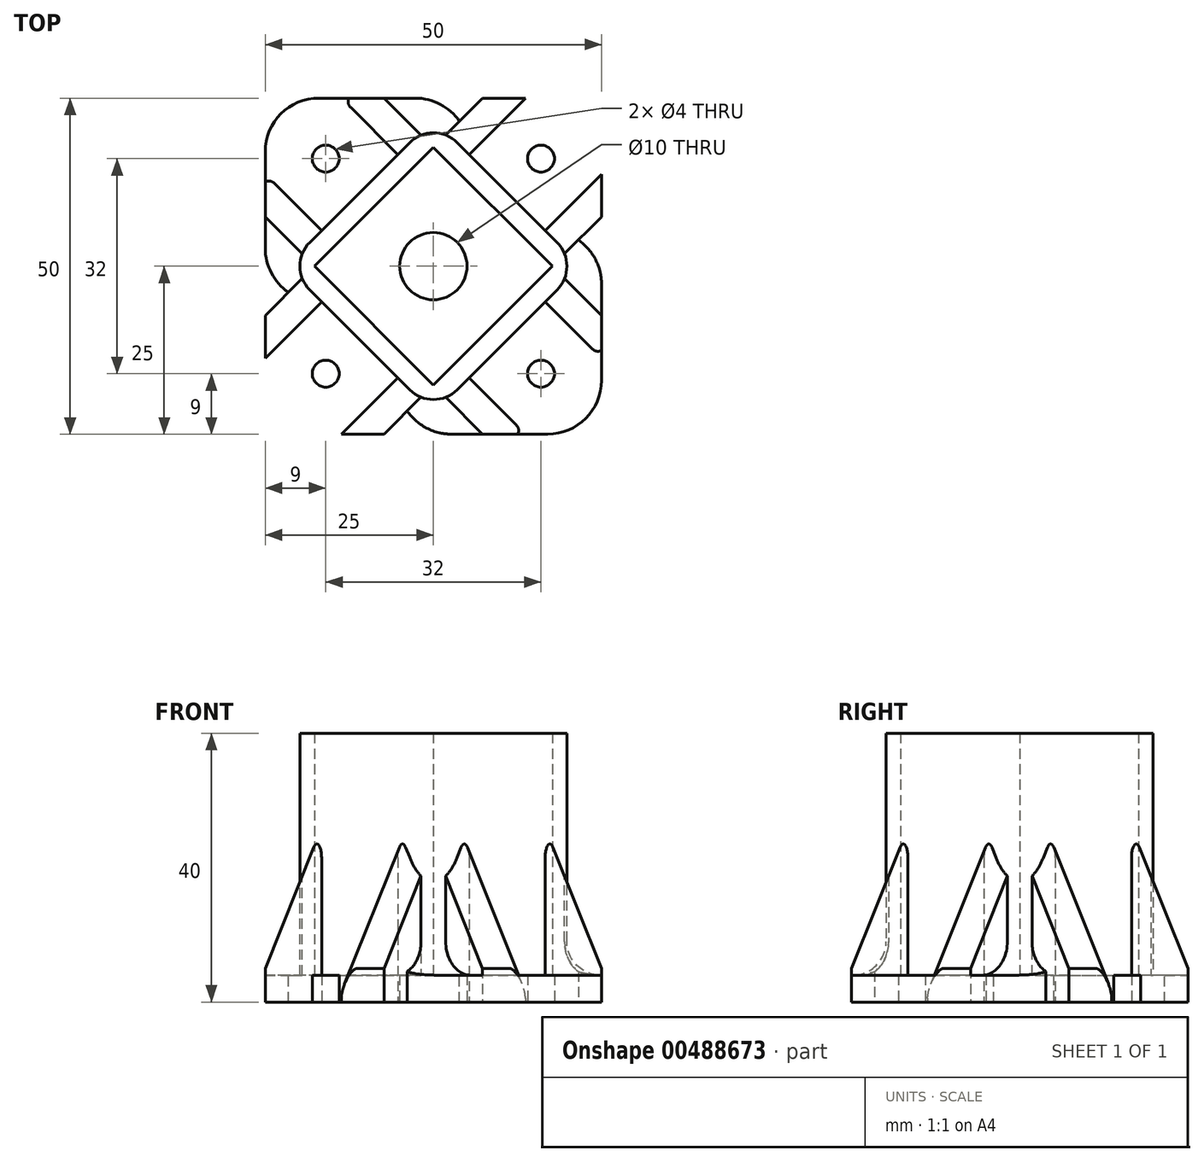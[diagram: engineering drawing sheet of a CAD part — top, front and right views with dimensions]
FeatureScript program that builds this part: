
annotation { "Feature Type Name" : "Feature", "Feature Type Description" : "" }
export const myFeature = defineFeature(function(context is Context, id is Id, definition is map)
    precondition{}
    {
        {
            var Q0;
            Q0=qCreatedBy(makeId("Top.planeOp"),FACE);
            var sketch = newSketch(context, id + "F0", { "sketchPlane" : qUnion([Q0])});
            skCircle(sketch, "E0", {"center": v(-16, 16) * mm, "radius": 2 * mm});
            skCircle(sketch, "E1.MirrorC", {"center": v(16, 16) * mm, "radius": 2 * mm});
            skCircle(sketch, "E2.MirrorC", {"center": v(16, -16) * mm, "radius": 2 * mm});
            skCircle(sketch, "E3.MirrorC", {"center": v(-16, -16) * mm, "radius": 2 * mm});
            skLineSegment(sketch, "E4.bottom", {"start": v(25, -25) * mm, "end": v(-25, -25) * mm});
            skLineSegment(sketch, "E4.top", {"start": v(25, 25) * mm, "end": v(-25, 25) * mm});
            skLineSegment(sketch, "E4.left", {"start": v(25, -25) * mm, "end": v(25, 25) * mm});
            skLineSegment(sketch, "E4.right", {"start": v(-25, -25) * mm, "end": v(-25, 25) * mm});
            skPoint(sketch, "E4.middle", {"position": v(0, 0) * mm});
            skLineSegment(sketch, "E5.bottom", {"start": v(17.68, 0) * mm, "end": v(0, -17.68) * mm});
            skLineSegment(sketch, "E5.top", {"start": v(0, 17.68) * mm, "end": v(-17.68, 0) * mm});
            skLineSegment(sketch, "E5.left", {"start": v(17.68, 0) * mm, "end": v(0, 17.68) * mm});
            skLineSegment(sketch, "E5.right", {"start": v(0, -17.68) * mm, "end": v(-17.68, 0) * mm});
            skCircle(sketch, "E6", {"center": v(0, 0) * mm, "radius": 5 * mm});
            skLineSegment(sketch, "E7", {"start": v(-21.92, 0) * mm, "end": v(0, -21.92) * mm});
            skLineSegment(sketch, "E8", {"start": v(0, 21.92) * mm, "end": v(21.92, 0) * mm});
            skLineSegment(sketch, "E9", {"start": v(0, -21.92) * mm, "end": v(2.12, -19.8) * mm});
            skLineSegment(sketch, "E10", {"start": v(-21.92, 0) * mm, "end": v(0, 21.92) * mm});
            skLineSegment(sketch, "E11", {"start": v(19.8, -2.12) * mm, "end": v(25, -7.32) * mm});
            skLineSegment(sketch, "E12", {"start": v(25, -13.69) * mm, "end": v(16.62, -5.3) * mm});
            skLineSegment(sketch, "E13", {"start": v(13.69, 25) * mm, "end": v(5.3, 16.62) * mm});
            skLineSegment(sketch, "E14", {"start": v(-25, 13.69) * mm, "end": v(-16.62, 5.3) * mm});
            skLineSegment(sketch, "E15", {"start": v(-13.69, -25) * mm, "end": v(-5.3, -16.62) * mm});
            skLineSegment(sketch, "E16.trimOffspring", {"start": v(16.62, 5.3) * mm, "end": v(25, 13.69) * mm});
            skLineSegment(sketch, "E17.trimOffspring", {"start": v(19.8, -2.12) * mm, "end": v(21.92, 0) * mm});
            skLineSegment(sketch, "E18.trimOffspring", {"start": v(5.3, -16.62) * mm, "end": v(13.69, -25) * mm});
            skLineSegment(sketch, "E19.trimOffspring", {"start": v(-16.62, -5.3) * mm, "end": v(-25, -13.69) * mm});
            skLineSegment(sketch, "E20.trimOffspring", {"start": v(-5.3, 16.62) * mm, "end": v(-13.69, 25) * mm});
            skLineSegment(sketch, "E21", {"start": v(19.8, 2.12) * mm, "end": v(25, 7.32) * mm});
            skLineSegment(sketch, "E22", {"start": v(-2.12, -19.8) * mm, "end": v(-7.32, -25) * mm});
            skLineSegment(sketch, "E23", {"start": v(-19.8, 2.12) * mm, "end": v(-25, 7.32) * mm});
            skLineSegment(sketch, "E24", {"start": v(-2.12, 19.8) * mm, "end": v(-7.32, 25) * mm});
            skLineSegment(sketch, "E25", {"start": v(-19.8, -2.12) * mm, "end": v(-25, -7.32) * mm});
            skLineSegment(sketch, "E26", {"start": v(2.12, -19.8) * mm, "end": v(7.32, -25) * mm});
            skLineSegment(sketch, "E27", {"start": v(2.12, 19.8) * mm, "end": v(7.32, 25) * mm});
            skLineSegment(sketch, "E28.trimOffspring", {"start": v(5.3, -16.62) * mm, "end": v(16.62, -5.3) * mm});
            skLineSegment(sketch, "E29", {"start": v(19.8, -2.12) * mm, "end": v(16.62, -5.3) * mm});
            skLineSegment(sketch, "E30", {"start": v(5.3, -16.62) * mm, "end": v(2.12, -19.8) * mm});
            skSolve(sketch);
        }
        {
            var Q0;
            Q0=makeQuery(id+"F0.imprint","IMPRINT",FACE,{"disambiguationData":[TD([[makeQuery(id+"F0.imprint","IMPRINT",EDGE,{"derivedFrom":sQuery(id+"F0.wireOp",EDGE,"E1.MirrorC")}),1.0]])]});
            var Q1;
            {var subQ0=sQuery(id+"F0.wireOp",EDGE,"E11");Q1=makeQuery(id+"F0.imprint","IMPRINT",FACE,{"disambiguationData":[TD([[makeQuery(id+"F0.imprint","IMPRINT",EDGE,{"derivedFrom":subQ0}),1.0]])]});}
            var Q2;
            Q2=makeQuery(id+"F0.imprint","IMPRINT",FACE,{"disambiguationData":[TD([[makeQuery(id+"F0.imprint","IMPRINT",EDGE,{"derivedFrom":sQuery(id+"F0.wireOp",EDGE,"E2.MirrorC")}),-1.0]])]});
            var Q3;
            {var subQ1=sQuery(id+"F0.wireOp",EDGE,"E9");Q3=makeQuery(id+"F0.imprint","IMPRINT",FACE,{"disambiguationData":[TD([[makeQuery(id+"F0.imprint","IMPRINT",EDGE,{"derivedFrom":subQ1}),-1.0]])]});}
            var Q4;
            Q4=makeQuery(id+"F0.imprint","IMPRINT",FACE,{"disambiguationData":[TD([[makeQuery(id+"F0.imprint","IMPRINT",EDGE,{"derivedFrom":sQuery(id+"F0.wireOp",EDGE,"E3.MirrorC")}),1.0]])]});
            var Q5;
            {var subQ3=sQuery(id+"F0.wireOp",EDGE,"E23");var subQ7=sQuery(id+"F0.wireOp",EDGE,"E4.right");var subQ8=makeQuery(id+"F0.imprint","INTERSECT",VERTEX,{"derivedFrom":[subQ7,subQ3]});Q5=makeQuery(id+"F0.imprint","IMPRINT",FACE,{"disambiguationData":[TD([[makeQuery(id+"F0.imprint","IMPRINT",EDGE,{"disambiguationData":[TD([[subQ8,1.0]])],"derivedFrom":subQ7}),-1.0]])]});}
            var Q6;
            Q6=makeQuery(id+"F0.imprint","IMPRINT",FACE,{"disambiguationData":[TD([[makeQuery(id+"F0.imprint","IMPRINT",EDGE,{"derivedFrom":sQuery(id+"F0.wireOp",EDGE,"E0")}),-1.0]])]});
            var Q7;
            {var subQ0=sQuery(id+"F0.wireOp",EDGE,"E20.trimOffspring");Q7=makeQuery(id+"F0.imprint","IMPRINT",FACE,{"disambiguationData":[TD([[makeQuery(id+"F0.imprint","IMPRINT",EDGE,{"derivedFrom":subQ0}),-1.0]])]});}
            var Q8;
            {var subQ3=sQuery(id+"F0.wireOp",EDGE,"E24");var subQ5=sQuery(id+"F0.wireOp",EDGE,"E4.top");var subQ6=makeQuery(id+"F0.imprint","INTERSECT",VERTEX,{"derivedFrom":[subQ5,subQ3]});Q8=makeQuery(id+"F0.imprint","IMPRINT",FACE,{"disambiguationData":[TD([[makeQuery(id+"F0.imprint","IMPRINT",EDGE,{"disambiguationData":[TD([[subQ6,1.0]])],"derivedFrom":subQ5}),1.0]])]});}
            var Q9;
            {var subQ0=sQuery(id+"F0.wireOp",EDGE,"E13");Q9=makeQuery(id+"F0.imprint","IMPRINT",FACE,{"disambiguationData":[TD([[makeQuery(id+"F0.imprint","IMPRINT",EDGE,{"derivedFrom":subQ0}),-1.0]])]});}
            var Q10;
            {var subQ0=sQuery(id+"F0.wireOp",EDGE,"E16.trimOffspring");Q10=makeQuery(id+"F0.imprint","IMPRINT",FACE,{"disambiguationData":[TD([[makeQuery(id+"F0.imprint","IMPRINT",EDGE,{"derivedFrom":subQ0}),-1.0]])]});}
            var Q11;
            {var subQ0=sQuery(id+"F0.wireOp",EDGE,"E11");Q11=makeQuery(id+"F0.imprint","IMPRINT",FACE,{"disambiguationData":[TD([[makeQuery(id+"F0.imprint","IMPRINT",EDGE,{"derivedFrom":subQ0}),-1.0]])]});}
            var Q12;
            {var subQ0=sQuery(id+"F0.wireOp",EDGE,"E18.trimOffspring");Q12=makeQuery(id+"F0.imprint","IMPRINT",FACE,{"disambiguationData":[TD([[makeQuery(id+"F0.imprint","IMPRINT",EDGE,{"derivedFrom":subQ0}),-1.0]])]});}
            var Q13;
            {var subQ0=sQuery(id+"F0.wireOp",EDGE,"E15");Q13=makeQuery(id+"F0.imprint","IMPRINT",FACE,{"disambiguationData":[TD([[makeQuery(id+"F0.imprint","IMPRINT",EDGE,{"derivedFrom":subQ0}),-1.0]])]});}
            var Q14;
            {var subQ0=sQuery(id+"F0.wireOp",EDGE,"E19.trimOffspring");Q14=makeQuery(id+"F0.imprint","IMPRINT",FACE,{"disambiguationData":[TD([[makeQuery(id+"F0.imprint","IMPRINT",EDGE,{"derivedFrom":subQ0}),-1.0]])]});}
            var Q15;
            {var subQ0=sQuery(id+"F0.wireOp",EDGE,"E14");Q15=makeQuery(id+"F0.imprint","IMPRINT",FACE,{"disambiguationData":[TD([[makeQuery(id+"F0.imprint","IMPRINT",EDGE,{"derivedFrom":subQ0}),-1.0]])]});}
            var Q16;
            Q16=makeQuery(id+"F0.imprint","IMPRINT",FACE,{"disambiguationData":[TD([[makeQuery(id+"F0.imprint","IMPRINT",EDGE,{"derivedFrom":sQuery(id+"F0.wireOp",EDGE,"E5.bottom")}),-1.0]])]});
            extrude(context, id + "F1", {"entities" : qUnion([Q0, Q1, Q2, Q3, Q4, Q5, Q6, Q7, Q8, Q9, Q10, Q11, Q12, Q13, Q14, Q15, Q16]), "depth" : 4 * mm});
        }
        {
            var Q0;
            Q0=makeQuery(id+"F0.imprint","IMPRINT",FACE,{"disambiguationData":[TD([[makeQuery(id+"F0.imprint","IMPRINT",EDGE,{"derivedFrom":sQuery(id+"F0.wireOp",EDGE,"E5.bottom")}),1.0]])]});
            extrude(context, id + "F2", {"entities" : qUnion([Q0]), "operationType" : NewBodyOperationType.ADD, "depth" : 40 * mm});
        }
        {
            var Q0;
            Q0=makeQuery(id+"F1.opExtrude","SWEPT_EDGE",EDGE,{"disambiguationData":[OSD([sQuery(id+"F0.wireOp",EDGE,"E4.top"),sQuery(id+"F0.wireOp",EDGE,"E4.right")])]});
            var Q1;
            Q1=makeQuery(id+"F1.opExtrude","SWEPT_EDGE",EDGE,{"disambiguationData":[OSD([sQuery(id+"F0.wireOp",EDGE,"E4.bottom"),sQuery(id+"F0.wireOp",EDGE,"E4.right")])]});
            var Q2;
            Q2=makeQuery(id+"F1.opExtrude","SWEPT_EDGE",EDGE,{"disambiguationData":[OSD([sQuery(id+"F0.wireOp",EDGE,"E4.bottom"),sQuery(id+"F0.wireOp",EDGE,"E4.left")])]});
            var Q3;
            Q3=makeQuery(id+"F1.opExtrude","SWEPT_EDGE",EDGE,{"disambiguationData":[OSD([sQuery(id+"F0.wireOp",EDGE,"E4.top"),sQuery(id+"F0.wireOp",EDGE,"E4.left")])]});
            fillet(context, id + "F3", {"entities" : qUnion([Q0, Q1, Q2, Q3]), "radius" : 8 * mm, "tangentPropagation" : true, "allowEdgeOverflow" : false});
        }
        {
            var Q0;
            {var subQ0=sQuery(id+"F0.wireOp",EDGE,"E11");Q0=makeQuery(id+"F0.imprint","IMPRINT",FACE,{"disambiguationData":[TD([[makeQuery(id+"F0.imprint","IMPRINT",EDGE,{"derivedFrom":subQ0}),-1.0]])]});}
            var Q1;
            {var subQ0=sQuery(id+"F0.wireOp",EDGE,"E18.trimOffspring");Q1=makeQuery(id+"F0.imprint","IMPRINT",FACE,{"disambiguationData":[TD([[makeQuery(id+"F0.imprint","IMPRINT",EDGE,{"derivedFrom":subQ0}),-1.0]])]});}
            var Q2;
            {var subQ0=sQuery(id+"F0.wireOp",EDGE,"E13");Q2=makeQuery(id+"F0.imprint","IMPRINT",FACE,{"disambiguationData":[TD([[makeQuery(id+"F0.imprint","IMPRINT",EDGE,{"derivedFrom":subQ0}),-1.0]])]});}
            var Q3;
            {var subQ0=sQuery(id+"F0.wireOp",EDGE,"E16.trimOffspring");Q3=makeQuery(id+"F0.imprint","IMPRINT",FACE,{"disambiguationData":[TD([[makeQuery(id+"F0.imprint","IMPRINT",EDGE,{"derivedFrom":subQ0}),-1.0]])]});}
            var Q4;
            {var subQ0=sQuery(id+"F0.wireOp",EDGE,"E15");Q4=makeQuery(id+"F0.imprint","IMPRINT",FACE,{"disambiguationData":[TD([[makeQuery(id+"F0.imprint","IMPRINT",EDGE,{"derivedFrom":subQ0}),-1.0]])]});}
            var Q5;
            {var subQ0=sQuery(id+"F0.wireOp",EDGE,"E19.trimOffspring");Q5=makeQuery(id+"F0.imprint","IMPRINT",FACE,{"disambiguationData":[TD([[makeQuery(id+"F0.imprint","IMPRINT",EDGE,{"derivedFrom":subQ0}),-1.0]])]});}
            var Q6;
            {var subQ0=sQuery(id+"F0.wireOp",EDGE,"E14");Q6=makeQuery(id+"F0.imprint","IMPRINT",FACE,{"disambiguationData":[TD([[makeQuery(id+"F0.imprint","IMPRINT",EDGE,{"derivedFrom":subQ0}),-1.0]])]});}
            var Q7;
            {var subQ0=sQuery(id+"F0.wireOp",EDGE,"E20.trimOffspring");Q7=makeQuery(id+"F0.imprint","IMPRINT",FACE,{"disambiguationData":[TD([[makeQuery(id+"F0.imprint","IMPRINT",EDGE,{"derivedFrom":subQ0}),-1.0]])]});}
            extrude(context, id + "F4", {"entities" : qUnion([Q0, Q1, Q2, Q3, Q4, Q5, Q6, Q7]), "operationType" : NewBodyOperationType.ADD, "depth" : 25 * mm});
        }
        {
            var Q0;
            {var subQ0=sQuery(id+"F0.wireOp",EDGE,"E4.bottom");Q0=makeQuery(id+"F4.opExtrude","CAP_EDGE",EDGE,{"disambiguationData":[OSD([subQ0]),TDD([makeQuery(id+"F0.imprint","IMPRINT",EDGE,{"disambiguationData":[TD([[makeQuery(id+"F0.imprint","INTERSECT",VERTEX,{"derivedFrom":[subQ0,sQuery(id+"F0.wireOp",EDGE,"E15")]}),1.0]])],"derivedFrom":subQ0})])],"isStart":false});}
            var Q1;
            {var subQ0=sQuery(id+"F0.wireOp",EDGE,"E4.bottom");Q1=makeQuery(id+"F4.opExtrude","CAP_EDGE",EDGE,{"disambiguationData":[OSD([subQ0]),TDD([makeQuery(id+"F0.imprint","IMPRINT",EDGE,{"disambiguationData":[TD([[makeQuery(id+"F0.imprint","INTERSECT",VERTEX,{"derivedFrom":[subQ0,sQuery(id+"F0.wireOp",EDGE,"E18.trimOffspring")]}),-1.0]])],"derivedFrom":subQ0})])],"isStart":false});}
            var Q2;
            {var subQ0=sQuery(id+"F0.wireOp",EDGE,"E4.right");Q2=makeQuery(id+"F4.opExtrude","CAP_EDGE",EDGE,{"disambiguationData":[OSD([subQ0]),TDD([makeQuery(id+"F0.imprint","IMPRINT",EDGE,{"disambiguationData":[TD([[makeQuery(id+"F0.imprint","INTERSECT",VERTEX,{"derivedFrom":[subQ0,sQuery(id+"F0.wireOp",EDGE,"E14")]}),1.0]])],"derivedFrom":subQ0})])],"isStart":false});}
            var Q3;
            {var subQ0=sQuery(id+"F0.wireOp",EDGE,"E4.right");Q3=makeQuery(id+"F4.opExtrude","CAP_EDGE",EDGE,{"disambiguationData":[OSD([subQ0]),TDD([makeQuery(id+"F0.imprint","IMPRINT",EDGE,{"disambiguationData":[TD([[makeQuery(id+"F0.imprint","INTERSECT",VERTEX,{"derivedFrom":[subQ0,sQuery(id+"F0.wireOp",EDGE,"E19.trimOffspring")]}),-1.0]])],"derivedFrom":subQ0})])],"isStart":false});}
            chamfer(context, id + "F5", {"entities" : qUnion([Q0, Q1, Q2, Q3]), "chamferType" : ChamferType.TWO_OFFSETS, "width1" : 20 * mm, "oppositeDirection" : false, "width2" : 8 * mm, "tangentPropagation" : true});
        }
        {
            var Q0;
            {var subQ0=sQuery(id+"F0.wireOp",EDGE,"E4.left");Q0=makeQuery(id+"F4.opExtrude","CAP_EDGE",EDGE,{"disambiguationData":[OSD([subQ0]),TDD([makeQuery(id+"F0.imprint","IMPRINT",EDGE,{"disambiguationData":[TD([[makeQuery(id+"F0.imprint","INTERSECT",VERTEX,{"derivedFrom":[subQ0,sQuery(id+"F0.wireOp",EDGE,"E11")]}),1.0]])],"derivedFrom":subQ0})])],"isStart":false});}
            var Q1;
            {var subQ0=sQuery(id+"F0.wireOp",EDGE,"E4.left");Q1=makeQuery(id+"F4.opExtrude","CAP_EDGE",EDGE,{"disambiguationData":[OSD([subQ0]),TDD([makeQuery(id+"F0.imprint","IMPRINT",EDGE,{"disambiguationData":[TD([[makeQuery(id+"F0.imprint","INTERSECT",VERTEX,{"derivedFrom":[subQ0,sQuery(id+"F0.wireOp",EDGE,"E16.trimOffspring")]}),1.0]])],"derivedFrom":subQ0})])],"isStart":false});}
            var Q2;
            {var subQ0=sQuery(id+"F0.wireOp",EDGE,"E4.top");Q2=makeQuery(id+"F4.opExtrude","CAP_EDGE",EDGE,{"disambiguationData":[OSD([subQ0]),TDD([makeQuery(id+"F0.imprint","IMPRINT",EDGE,{"disambiguationData":[TD([[makeQuery(id+"F0.imprint","INTERSECT",VERTEX,{"derivedFrom":[subQ0,sQuery(id+"F0.wireOp",EDGE,"E13")]}),-1.0]])],"derivedFrom":subQ0})])],"isStart":false});}
            var Q3;
            {var subQ0=sQuery(id+"F0.wireOp",EDGE,"E4.top");Q3=makeQuery(id+"F4.opExtrude","CAP_EDGE",EDGE,{"disambiguationData":[OSD([subQ0]),TDD([makeQuery(id+"F0.imprint","IMPRINT",EDGE,{"disambiguationData":[TD([[makeQuery(id+"F0.imprint","INTERSECT",VERTEX,{"derivedFrom":[subQ0,sQuery(id+"F0.wireOp",EDGE,"E20.trimOffspring")]}),1.0]])],"derivedFrom":subQ0})])],"isStart":false});}
            chamfer(context, id + "F6", {"entities" : qUnion([Q0, Q1, Q2, Q3]), "chamferType" : ChamferType.TWO_OFFSETS, "width1" : 8 * mm, "oppositeDirection" : false, "width2" : 20 * mm});
        }
        {
            var Q0;
            {var subQ0=sQuery(id+"F0.wireOp",EDGE,"E18.trimOffspring");var subQ1=sQuery(id+"F0.wireOp",EDGE,"E4.bottom");Q0=makeQuery(id+"F5.opChamfer","BLEND_EDGE",EDGE,{"blendedFrom":[makeQuery(id+"F4.opExtrude","CAP_EDGE",EDGE,{"disambiguationData":[OSD([subQ1]),TDD([makeQuery(id+"F0.imprint","IMPRINT",EDGE,{"disambiguationData":[TD([[makeQuery(id+"F0.imprint","INTERSECT",VERTEX,{"derivedFrom":[subQ1,subQ0]}),-1.0]])],"derivedFrom":subQ1})])],"isStart":false}),makeQuery(id+"F4.opExtrude","SWEPT_FACE",FACE,{"disambiguationData":[OSD([subQ0])]})],"blendedInto":[makeQuery(id+"F4.opExtrude","SWEPT_FACE",FACE,{"disambiguationData":[OSD([subQ0])]})]});}
            var Q1;
            {var subQ0=sQuery(id+"F0.wireOp",EDGE,"E12");var subQ1=sQuery(id+"F0.wireOp",EDGE,"E4.left");Q1=makeQuery(id+"F6.opChamfer","BLEND_EDGE",EDGE,{"blendedFrom":[makeQuery(id+"F4.opExtrude","CAP_EDGE",EDGE,{"disambiguationData":[OSD([subQ1]),TDD([makeQuery(id+"F0.imprint","IMPRINT",EDGE,{"disambiguationData":[TD([[makeQuery(id+"F0.imprint","INTERSECT",VERTEX,{"derivedFrom":[subQ1,sQuery(id+"F0.wireOp",EDGE,"E11")]}),1.0]])],"derivedFrom":subQ1})])],"isStart":false}),makeQuery(id+"F4.opExtrude","SWEPT_FACE",FACE,{"disambiguationData":[OSD([subQ0])]})],"blendedInto":[makeQuery(id+"F4.opExtrude","SWEPT_FACE",FACE,{"disambiguationData":[OSD([subQ0])]})]});}
            var Q2;
            {var subQ0=sQuery(id+"F0.wireOp",EDGE,"E16.trimOffspring");var subQ1=sQuery(id+"F0.wireOp",EDGE,"E4.left");Q2=makeQuery(id+"F6.opChamfer","BLEND_EDGE",EDGE,{"blendedFrom":[makeQuery(id+"F4.opExtrude","CAP_EDGE",EDGE,{"disambiguationData":[OSD([subQ1]),TDD([makeQuery(id+"F0.imprint","IMPRINT",EDGE,{"disambiguationData":[TD([[makeQuery(id+"F0.imprint","INTERSECT",VERTEX,{"derivedFrom":[subQ1,subQ0]}),1.0]])],"derivedFrom":subQ1})])],"isStart":false}),makeQuery(id+"F4.opExtrude","SWEPT_FACE",FACE,{"disambiguationData":[OSD([subQ0])]})],"blendedInto":[makeQuery(id+"F4.opExtrude","SWEPT_FACE",FACE,{"disambiguationData":[OSD([subQ0])]})]});}
            var Q3;
            {var subQ0=sQuery(id+"F0.wireOp",EDGE,"E13");var subQ1=sQuery(id+"F0.wireOp",EDGE,"E4.top");Q3=makeQuery(id+"F6.opChamfer","BLEND_EDGE",EDGE,{"blendedFrom":[makeQuery(id+"F4.opExtrude","CAP_EDGE",EDGE,{"disambiguationData":[OSD([subQ1]),TDD([makeQuery(id+"F0.imprint","IMPRINT",EDGE,{"disambiguationData":[TD([[makeQuery(id+"F0.imprint","INTERSECT",VERTEX,{"derivedFrom":[subQ1,subQ0]}),-1.0]])],"derivedFrom":subQ1})])],"isStart":false}),makeQuery(id+"F4.opExtrude","SWEPT_FACE",FACE,{"disambiguationData":[OSD([subQ0])]})],"blendedInto":[makeQuery(id+"F4.opExtrude","SWEPT_FACE",FACE,{"disambiguationData":[OSD([subQ0])]})]});}
            var Q4;
            {var subQ0=sQuery(id+"F0.wireOp",EDGE,"E20.trimOffspring");var subQ1=sQuery(id+"F0.wireOp",EDGE,"E4.top");Q4=makeQuery(id+"F6.opChamfer","BLEND_EDGE",EDGE,{"blendedFrom":[makeQuery(id+"F4.opExtrude","CAP_EDGE",EDGE,{"disambiguationData":[OSD([subQ1]),TDD([makeQuery(id+"F0.imprint","IMPRINT",EDGE,{"disambiguationData":[TD([[makeQuery(id+"F0.imprint","INTERSECT",VERTEX,{"derivedFrom":[subQ1,subQ0]}),1.0]])],"derivedFrom":subQ1})])],"isStart":false}),makeQuery(id+"F4.opExtrude","SWEPT_FACE",FACE,{"disambiguationData":[OSD([subQ0])]})],"blendedInto":[makeQuery(id+"F4.opExtrude","SWEPT_FACE",FACE,{"disambiguationData":[OSD([subQ0])]})]});}
            var Q5;
            {var subQ0=sQuery(id+"F0.wireOp",EDGE,"E14");var subQ1=sQuery(id+"F0.wireOp",EDGE,"E4.right");Q5=makeQuery(id+"F5.opChamfer","BLEND_EDGE",EDGE,{"blendedFrom":[makeQuery(id+"F4.opExtrude","CAP_EDGE",EDGE,{"disambiguationData":[OSD([subQ1]),TDD([makeQuery(id+"F0.imprint","IMPRINT",EDGE,{"disambiguationData":[TD([[makeQuery(id+"F0.imprint","INTERSECT",VERTEX,{"derivedFrom":[subQ1,subQ0]}),1.0]])],"derivedFrom":subQ1})])],"isStart":false}),makeQuery(id+"F4.opExtrude","SWEPT_FACE",FACE,{"disambiguationData":[OSD([subQ0])]})],"blendedInto":[makeQuery(id+"F4.opExtrude","SWEPT_FACE",FACE,{"disambiguationData":[OSD([subQ0])]})]});}
            var Q6;
            {var subQ0=sQuery(id+"F0.wireOp",EDGE,"E19.trimOffspring");var subQ1=sQuery(id+"F0.wireOp",EDGE,"E4.right");Q6=makeQuery(id+"F5.opChamfer","BLEND_EDGE",EDGE,{"blendedFrom":[makeQuery(id+"F4.opExtrude","CAP_EDGE",EDGE,{"disambiguationData":[OSD([subQ1]),TDD([makeQuery(id+"F0.imprint","IMPRINT",EDGE,{"disambiguationData":[TD([[makeQuery(id+"F0.imprint","INTERSECT",VERTEX,{"derivedFrom":[subQ1,subQ0]}),-1.0]])],"derivedFrom":subQ1})])],"isStart":false}),makeQuery(id+"F4.opExtrude","SWEPT_FACE",FACE,{"disambiguationData":[OSD([subQ0])]})],"blendedInto":[makeQuery(id+"F4.opExtrude","SWEPT_FACE",FACE,{"disambiguationData":[OSD([subQ0])]})]});}
            var Q7;
            {var subQ0=sQuery(id+"F0.wireOp",EDGE,"E15");var subQ1=sQuery(id+"F0.wireOp",EDGE,"E4.bottom");Q7=makeQuery(id+"F5.opChamfer","BLEND_EDGE",EDGE,{"blendedFrom":[makeQuery(id+"F4.opExtrude","CAP_EDGE",EDGE,{"disambiguationData":[OSD([subQ1]),TDD([makeQuery(id+"F0.imprint","IMPRINT",EDGE,{"disambiguationData":[TD([[makeQuery(id+"F0.imprint","INTERSECT",VERTEX,{"derivedFrom":[subQ1,subQ0]}),1.0]])],"derivedFrom":subQ1})])],"isStart":false}),makeQuery(id+"F4.opExtrude","SWEPT_FACE",FACE,{"disambiguationData":[OSD([subQ0])]})],"blendedInto":[makeQuery(id+"F4.opExtrude","SWEPT_FACE",FACE,{"disambiguationData":[OSD([subQ0])]})]});}
            fillet(context, id + "F7", {"entities" : qUnion([Q0, Q1, Q2, Q3, Q4, Q5, Q6, Q7]), "radius" : 1 * mm, "tangentPropagation" : true, "allowEdgeOverflow" : false});
        }
        {
            var Q0;
            Q0=makeQuery(id+"F2.opExtrude","SWEPT_EDGE",EDGE,{"disambiguationData":[OSD([sQuery(id+"F0.wireOp",EDGE,"E7"),sQuery(id+"F0.wireOp",EDGE,"E9")])]});
            var Q1;
            Q1=makeQuery(id+"F2.opExtrude","SWEPT_EDGE",EDGE,{"disambiguationData":[OSD([sQuery(id+"F0.wireOp",EDGE,"E8"),sQuery(id+"F0.wireOp",EDGE,"E17.trimOffspring")])]});
            var Q2;
            Q2=makeQuery(id+"F2.opExtrude","SWEPT_EDGE",EDGE,{"disambiguationData":[OSD([sQuery(id+"F0.wireOp",EDGE,"E8"),sQuery(id+"F0.wireOp",EDGE,"E10")])]});
            var Q3;
            Q3=makeQuery(id+"F2.opExtrude","SWEPT_EDGE",EDGE,{"disambiguationData":[OSD([sQuery(id+"F0.wireOp",EDGE,"E7"),sQuery(id+"F0.wireOp",EDGE,"E10")])]});
            fillet(context, id + "F8", {"entities" : qUnion([Q0, Q1, Q2, Q3]), "radius" : 5 * mm, "tangentPropagation" : true, "allowEdgeOverflow" : false});
        }
        {
            var Q0;
            {var subQ0=sQuery(id+"F0.wireOp",EDGE,"E8");Q0=makeQuery(id+"F4.boolean.opBoolean","SPLIT",EDGE,{"disambiguationData":[TD([makeQuery(id+"F4.opExtrude","SWEPT_FACE",FACE,{"disambiguationData":[OSD([sQuery(id+"F0.wireOp",EDGE,"E13")])]})])],"derivedFrom":makeQuery(id+"F1.opExtrude","CAP_EDGE",EDGE,{"disambiguationData":[OSD([subQ0])],"isStart":false})});}
            var Q1;
            {var subQ0=sQuery(id+"F0.wireOp",EDGE,"E10");Q1=makeQuery(id+"F4.boolean.opBoolean","SPLIT",EDGE,{"disambiguationData":[TD([makeQuery(id+"F4.opExtrude","SWEPT_FACE",FACE,{"disambiguationData":[OSD([sQuery(id+"F0.wireOp",EDGE,"E14")])]})])],"derivedFrom":makeQuery(id+"F1.opExtrude","CAP_EDGE",EDGE,{"disambiguationData":[OSD([subQ0])],"isStart":false})});}
            var Q2;
            {var subQ0=sQuery(id+"F0.wireOp",EDGE,"E10");var subQ1=sQuery(id+"F0.wireOp",EDGE,"E23");var subQ2=sQuery(id+"F0.wireOp",EDGE,"E4.right");var subQ4=sQuery(id+"F0.wireOp",EDGE,"E7");Q2=makeQuery(id+"F8.opFillet","BLEND_EDGE",EDGE,{"blendedFrom":[makeQuery(id+"F2.opExtrude","SWEPT_EDGE",EDGE,{"disambiguationData":[OSD([subQ4,subQ0])]}),makeQuery(id+"F4.boolean.opBoolean","SPLIT",FACE,{"disambiguationData":[TD([makeQuery(id+"F4.opExtrude","SWEPT_FACE",FACE,{"disambiguationData":[OSD([subQ1])]})])],"derivedFrom":makeQuery(id+"F1.opExtrude","CAP_FACE",FACE,{"disambiguationData":[OSD([sQuery(id+"F0.wireOp",EDGE,"E0"),sQuery(id+"F0.wireOp",EDGE,"E1.MirrorC"),sQuery(id+"F0.wireOp",EDGE,"E2.MirrorC"),sQuery(id+"F0.wireOp",EDGE,"E3.MirrorC"),sQuery(id+"F0.wireOp",EDGE,"E4.bottom"),sQuery(id+"F0.wireOp",EDGE,"E4.top"),sQuery(id+"F0.wireOp",EDGE,"E4.left"),subQ2,subQ4,sQuery(id+"F0.wireOp",EDGE,"E8"),sQuery(id+"F0.wireOp",EDGE,"E9"),subQ0,sQuery(id+"F0.wireOp",EDGE,"E17.trimOffspring"),sQuery(id+"F0.wireOp",EDGE,"E28.trimOffspring"),sQuery(id+"F0.wireOp",EDGE,"E29"),sQuery(id+"F0.wireOp",EDGE,"E30")])],"isStart":false})})],"blendedInto":[makeQuery(id+"F4.boolean.opBoolean","SPLIT",FACE,{"disambiguationData":[TD([makeQuery(id+"F4.opExtrude","SWEPT_FACE",FACE,{"disambiguationData":[OSD([subQ1])]})])],"derivedFrom":makeQuery(id+"F1.opExtrude","CAP_FACE",FACE,{"disambiguationData":[OSD([sQuery(id+"F0.wireOp",EDGE,"E0"),sQuery(id+"F0.wireOp",EDGE,"E1.MirrorC"),sQuery(id+"F0.wireOp",EDGE,"E2.MirrorC"),sQuery(id+"F0.wireOp",EDGE,"E3.MirrorC"),sQuery(id+"F0.wireOp",EDGE,"E4.bottom"),sQuery(id+"F0.wireOp",EDGE,"E4.top"),sQuery(id+"F0.wireOp",EDGE,"E4.left"),subQ2,subQ4,sQuery(id+"F0.wireOp",EDGE,"E8"),sQuery(id+"F0.wireOp",EDGE,"E9"),subQ0,sQuery(id+"F0.wireOp",EDGE,"E17.trimOffspring"),sQuery(id+"F0.wireOp",EDGE,"E28.trimOffspring"),sQuery(id+"F0.wireOp",EDGE,"E29"),sQuery(id+"F0.wireOp",EDGE,"E30")])],"isStart":false})})]});}
            var Q3;
            {var subQ0=sQuery(id+"F0.wireOp",EDGE,"E4.top");var subQ2=sQuery(id+"F0.wireOp",EDGE,"E8");var subQ3=sQuery(id+"F0.wireOp",EDGE,"E10");var subQ4=sQuery(id+"F0.wireOp",EDGE,"E24");Q3=makeQuery(id+"F8.opFillet","BLEND_EDGE",EDGE,{"blendedFrom":[makeQuery(id+"F2.opExtrude","SWEPT_EDGE",EDGE,{"disambiguationData":[OSD([subQ2,subQ3])]}),makeQuery(id+"F4.boolean.opBoolean","SPLIT",FACE,{"disambiguationData":[TD([makeQuery(id+"F4.opExtrude","SWEPT_FACE",FACE,{"disambiguationData":[OSD([subQ4])]})])],"derivedFrom":makeQuery(id+"F1.opExtrude","CAP_FACE",FACE,{"disambiguationData":[OSD([sQuery(id+"F0.wireOp",EDGE,"E0"),sQuery(id+"F0.wireOp",EDGE,"E1.MirrorC"),sQuery(id+"F0.wireOp",EDGE,"E2.MirrorC"),sQuery(id+"F0.wireOp",EDGE,"E3.MirrorC"),sQuery(id+"F0.wireOp",EDGE,"E4.bottom"),subQ0,sQuery(id+"F0.wireOp",EDGE,"E4.left"),sQuery(id+"F0.wireOp",EDGE,"E4.right"),sQuery(id+"F0.wireOp",EDGE,"E7"),subQ2,sQuery(id+"F0.wireOp",EDGE,"E9"),subQ3,sQuery(id+"F0.wireOp",EDGE,"E17.trimOffspring"),sQuery(id+"F0.wireOp",EDGE,"E28.trimOffspring"),sQuery(id+"F0.wireOp",EDGE,"E29"),sQuery(id+"F0.wireOp",EDGE,"E30")])],"isStart":false})})],"blendedInto":[makeQuery(id+"F4.boolean.opBoolean","SPLIT",FACE,{"disambiguationData":[TD([makeQuery(id+"F4.opExtrude","SWEPT_FACE",FACE,{"disambiguationData":[OSD([subQ4])]})])],"derivedFrom":makeQuery(id+"F1.opExtrude","CAP_FACE",FACE,{"disambiguationData":[OSD([sQuery(id+"F0.wireOp",EDGE,"E0"),sQuery(id+"F0.wireOp",EDGE,"E1.MirrorC"),sQuery(id+"F0.wireOp",EDGE,"E2.MirrorC"),sQuery(id+"F0.wireOp",EDGE,"E3.MirrorC"),sQuery(id+"F0.wireOp",EDGE,"E4.bottom"),subQ0,sQuery(id+"F0.wireOp",EDGE,"E4.left"),sQuery(id+"F0.wireOp",EDGE,"E4.right"),sQuery(id+"F0.wireOp",EDGE,"E7"),subQ2,sQuery(id+"F0.wireOp",EDGE,"E9"),subQ3,sQuery(id+"F0.wireOp",EDGE,"E17.trimOffspring"),sQuery(id+"F0.wireOp",EDGE,"E28.trimOffspring"),sQuery(id+"F0.wireOp",EDGE,"E29"),sQuery(id+"F0.wireOp",EDGE,"E30")])],"isStart":false})})]});}
            var Q4;
            {var subQ0=sQuery(id+"F0.wireOp",EDGE,"E7");Q4=makeQuery(id+"F4.boolean.opBoolean","SPLIT",EDGE,{"disambiguationData":[TD([makeQuery(id+"F4.opExtrude","SWEPT_FACE",FACE,{"disambiguationData":[OSD([sQuery(id+"F0.wireOp",EDGE,"E15")])]})])],"derivedFrom":makeQuery(id+"F1.opExtrude","CAP_EDGE",EDGE,{"disambiguationData":[OSD([subQ0])],"isStart":false})});}
            var Q5;
            {var subQ0=sQuery(id+"F0.wireOp",EDGE,"E4.bottom");var subQ2=sQuery(id+"F0.wireOp",EDGE,"E30");var subQ3=sQuery(id+"F0.wireOp",EDGE,"E29");var subQ4=sQuery(id+"F0.wireOp",EDGE,"E28.trimOffspring");var subQ5=sQuery(id+"F0.wireOp",EDGE,"E17.trimOffspring");var subQ6=sQuery(id+"F0.wireOp",EDGE,"E9");var subQ7=sQuery(id+"F0.wireOp",EDGE,"E22");var subQ8=sQuery(id+"F0.wireOp",EDGE,"E7");Q5=makeQuery(id+"F8.opFillet","BLEND_EDGE",EDGE,{"blendedFrom":[makeQuery(id+"F2.opExtrude","SWEPT_EDGE",EDGE,{"disambiguationData":[OSD([subQ8,subQ6])]}),makeQuery(id+"F4.boolean.opBoolean","SPLIT",FACE,{"disambiguationData":[TD([makeQuery(id+"F4.opExtrude","SWEPT_FACE",FACE,{"disambiguationData":[OSD([subQ7])]})])],"derivedFrom":makeQuery(id+"F1.opExtrude","CAP_FACE",FACE,{"disambiguationData":[OSD([sQuery(id+"F0.wireOp",EDGE,"E0"),sQuery(id+"F0.wireOp",EDGE,"E1.MirrorC"),sQuery(id+"F0.wireOp",EDGE,"E2.MirrorC"),sQuery(id+"F0.wireOp",EDGE,"E3.MirrorC"),subQ0,sQuery(id+"F0.wireOp",EDGE,"E4.top"),sQuery(id+"F0.wireOp",EDGE,"E4.left"),sQuery(id+"F0.wireOp",EDGE,"E4.right"),subQ8,sQuery(id+"F0.wireOp",EDGE,"E8"),subQ6,sQuery(id+"F0.wireOp",EDGE,"E10"),subQ5,subQ4,subQ3,subQ2])],"isStart":false})})],"blendedInto":[makeQuery(id+"F4.boolean.opBoolean","SPLIT",FACE,{"disambiguationData":[TD([makeQuery(id+"F4.opExtrude","SWEPT_FACE",FACE,{"disambiguationData":[OSD([subQ7])]})])],"derivedFrom":makeQuery(id+"F1.opExtrude","CAP_FACE",FACE,{"disambiguationData":[OSD([sQuery(id+"F0.wireOp",EDGE,"E0"),sQuery(id+"F0.wireOp",EDGE,"E1.MirrorC"),sQuery(id+"F0.wireOp",EDGE,"E2.MirrorC"),sQuery(id+"F0.wireOp",EDGE,"E3.MirrorC"),subQ0,sQuery(id+"F0.wireOp",EDGE,"E4.top"),sQuery(id+"F0.wireOp",EDGE,"E4.left"),sQuery(id+"F0.wireOp",EDGE,"E4.right"),subQ8,sQuery(id+"F0.wireOp",EDGE,"E8"),subQ6,sQuery(id+"F0.wireOp",EDGE,"E10"),subQ5,subQ4,subQ3,subQ2])],"isStart":false})})]});}
            var Q6;
            {var subQ0=sQuery(id+"F0.wireOp",EDGE,"E30");var subQ1=sQuery(id+"F0.wireOp",EDGE,"E29");var subQ2=sQuery(id+"F0.wireOp",EDGE,"E28.trimOffspring");var subQ3=sQuery(id+"F0.wireOp",EDGE,"E17.trimOffspring");var subQ4=sQuery(id+"F0.wireOp",EDGE,"E9");Q6=makeQuery(id+"F4.boolean.opBoolean","SPLIT",EDGE,{"disambiguationData":[TD([makeQuery(id+"F4.opExtrude","SWEPT_FACE",FACE,{"disambiguationData":[OSD([sQuery(id+"F0.wireOp",EDGE,"E12")])]})])],"derivedFrom":makeQuery(id+"F1.opExtrude","CAP_EDGE",EDGE,{"disambiguationData":[OSD([subQ4,subQ3,subQ2,subQ1,subQ0])],"isStart":false})});}
            var Q7;
            {var subQ0=sQuery(id+"F0.wireOp",EDGE,"E11");var subQ1=sQuery(id+"F0.wireOp",EDGE,"E4.left");var subQ2=sQuery(id+"F0.wireOp",EDGE,"E30");var subQ3=sQuery(id+"F0.wireOp",EDGE,"E29");var subQ4=sQuery(id+"F0.wireOp",EDGE,"E28.trimOffspring");var subQ5=sQuery(id+"F0.wireOp",EDGE,"E17.trimOffspring");var subQ6=sQuery(id+"F0.wireOp",EDGE,"E9");var subQ7=sQuery(id+"F0.wireOp",EDGE,"E8");Q7=makeQuery(id+"F8.opFillet","BLEND_EDGE",EDGE,{"blendedFrom":[makeQuery(id+"F2.opExtrude","SWEPT_EDGE",EDGE,{"disambiguationData":[OSD([subQ7,subQ5])]}),makeQuery(id+"F4.boolean.opBoolean","SPLIT",FACE,{"disambiguationData":[TD([makeQuery(id+"F4.opExtrude","SWEPT_FACE",FACE,{"disambiguationData":[OSD([subQ0])]})])],"derivedFrom":makeQuery(id+"F1.opExtrude","CAP_FACE",FACE,{"disambiguationData":[OSD([sQuery(id+"F0.wireOp",EDGE,"E0"),sQuery(id+"F0.wireOp",EDGE,"E1.MirrorC"),sQuery(id+"F0.wireOp",EDGE,"E2.MirrorC"),sQuery(id+"F0.wireOp",EDGE,"E3.MirrorC"),sQuery(id+"F0.wireOp",EDGE,"E4.bottom"),sQuery(id+"F0.wireOp",EDGE,"E4.top"),subQ1,sQuery(id+"F0.wireOp",EDGE,"E4.right"),sQuery(id+"F0.wireOp",EDGE,"E7"),subQ7,subQ6,sQuery(id+"F0.wireOp",EDGE,"E10"),subQ5,subQ4,subQ3,subQ2])],"isStart":false})})],"blendedInto":[makeQuery(id+"F4.boolean.opBoolean","SPLIT",FACE,{"disambiguationData":[TD([makeQuery(id+"F4.opExtrude","SWEPT_FACE",FACE,{"disambiguationData":[OSD([subQ0])]})])],"derivedFrom":makeQuery(id+"F1.opExtrude","CAP_FACE",FACE,{"disambiguationData":[OSD([sQuery(id+"F0.wireOp",EDGE,"E0"),sQuery(id+"F0.wireOp",EDGE,"E1.MirrorC"),sQuery(id+"F0.wireOp",EDGE,"E2.MirrorC"),sQuery(id+"F0.wireOp",EDGE,"E3.MirrorC"),sQuery(id+"F0.wireOp",EDGE,"E4.bottom"),sQuery(id+"F0.wireOp",EDGE,"E4.top"),subQ1,sQuery(id+"F0.wireOp",EDGE,"E4.right"),sQuery(id+"F0.wireOp",EDGE,"E7"),subQ7,subQ6,sQuery(id+"F0.wireOp",EDGE,"E10"),subQ5,subQ4,subQ3,subQ2])],"isStart":false})})]});}
            fillet(context, id + "F9", {"entities" : qUnion([Q0, Q1, Q2, Q3, Q4, Q5, Q6, Q7]), "radius" : 5 * mm, "tangentPropagation" : true, "allowEdgeOverflow" : false});
        }
    });
